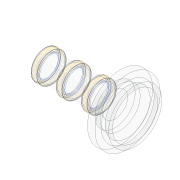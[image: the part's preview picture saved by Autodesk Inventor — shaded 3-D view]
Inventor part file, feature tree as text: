
AUTODESK INVENTOR PART (.ipt)
format: ipt  version: 2021 (Build 250183000, 183)  size: 539,648 bytes
history: native  units: in
note: dims shown in document units (in); Inventor stores cm internally (conversion verified against a paired STEP export)
features: projected_geometry x8, revolve x3, sketch x3, chamfer x2, split x2, fillet x1
ambient origin geometry x8: Origin, YZ Plane, XZ Plane, XY Plane, X Axis, Y Axis, Z Axis, Center Point
bodies: Solid1 (feature_tree), Solid4 (feature_tree)
feature tree (19):
  revolve  "Revolution1"  [1 undecoded]
  revolve  "Revolution2"  [1 undecoded]
  revolve  "Revolution5"  [1 undecoded]
  chamfer  "Chamfer1"  Distance=0.2559in
  chamfer  "Chamfer2"  Angle=90.0deg  [1 undecoded]
  fillet  "Fillet6"  [1 undecoded]
  split  "Split1"
  split  "Split2"
  sketch  "Sketch1"  dims[d2=0.0591in d3=0.0591in]
  sketch  "Sketch2"  dims[d4=0.0591in d5=0.0591in]
  projected_geometry  "Projected Loop1"
  projected_geometry  "Projected Loop2"
  projected_geometry  "Projected Loop3"
  projected_geometry  "Projected Loop4"
  projected_geometry  "Projected Loop5"
  sketch  "Sketch3"  dims[d9=0.1378in d10=0.1378in d14=0.2559in d15=90.0deg d31=90.0deg d52=90.0deg d53=0.0059in d54=0.0787in d55=45.0deg d57=0.0059in d58=0.0787in d59=45.0deg d60=0.2087in d61=0.1772in d62=0.0591in d63=0.0984in d64=0.0394in d65=0.1575in d73=0.0118in d74=0.0118in d75=0.0217in d76=0.0118in d77=0.0118in d78=0.0217in d79=0.0118in d80=0.0118in d81=0.0217in d82=0.037in d83=0.0079in d84=0.0079in d85=0.0059in d86=1.1811in d88=0.1969in d89=0.3937in d91=0.3937in d94=0.002in]
  projected_geometry  "Project Cut Edges1"
  projected_geometry  "Project Cut Edges2"
  projected_geometry  "Project Cut Edges3"
note: 5 required parameter values undecoded (feature->parameter linkage not recoverable at this tier; creation-order binding heuristic only, values carry confidence <= 0.55)